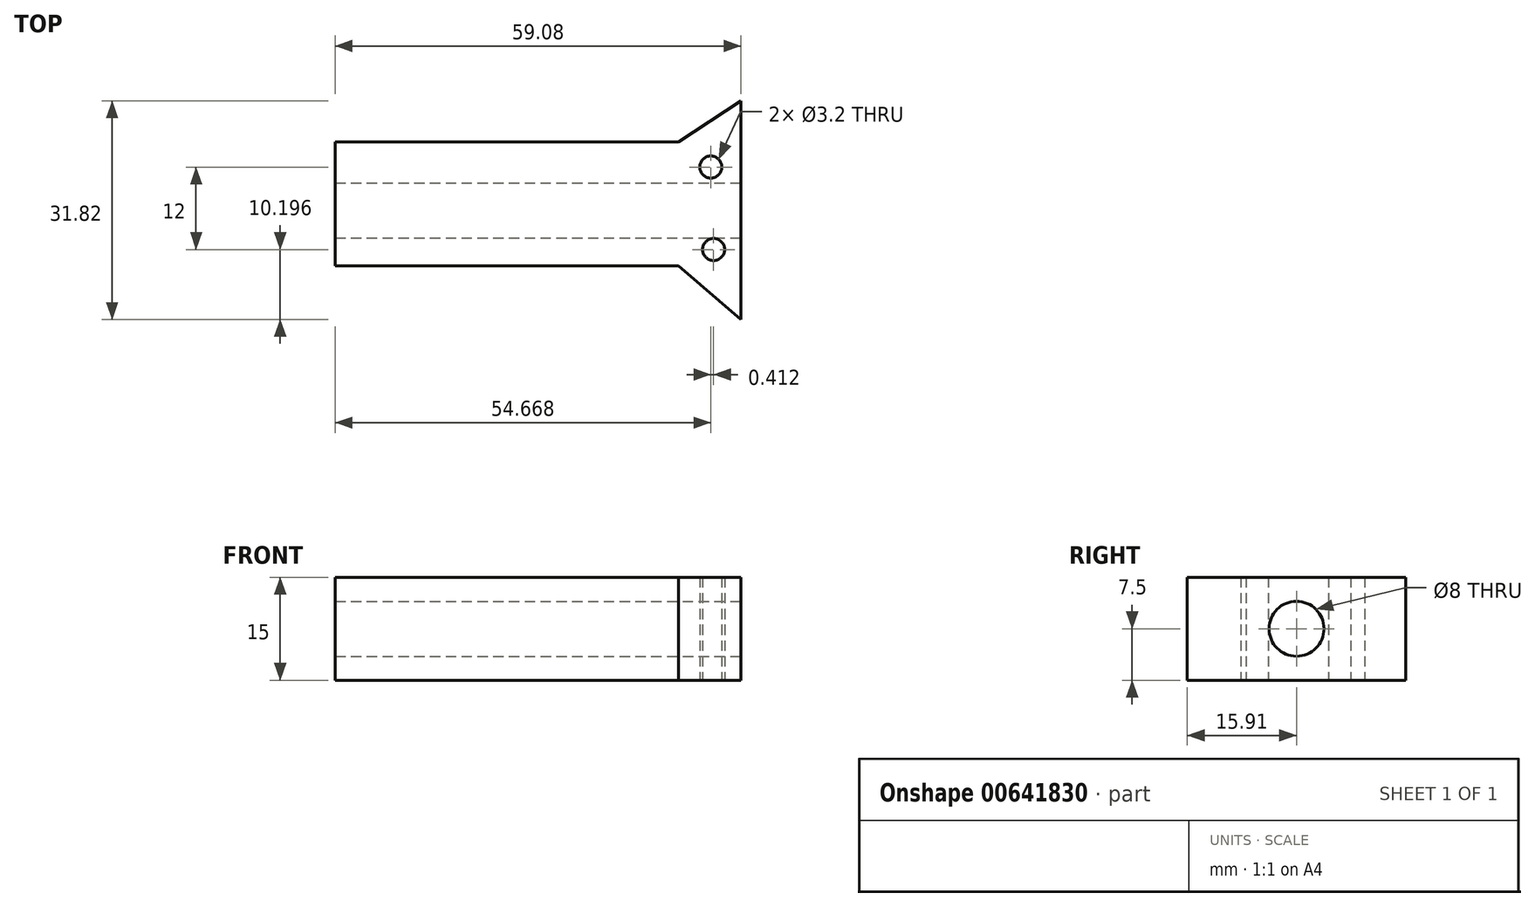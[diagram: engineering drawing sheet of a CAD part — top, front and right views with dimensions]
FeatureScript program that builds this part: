
annotation { "Feature Type Name" : "Feature", "Feature Type Description" : "" }
export const myFeature = defineFeature(function(context is Context, id is Id, definition is map)
    precondition{}
    {
        {
            var Q0;
            Q0=qCreatedBy(makeId("Top.planeOp"),FACE);
            var sketch = newSketch(context, id + "F0", { "sketchPlane" : qUnion([Q0])});
            skLineSegment(sketch, "E0.left", {"start": v(-5.08, -22.24) * mm, "end": v(-5.08, -4.24) * mm});
            skLineSegment(sketch, "E0.right", {"start": v(4, -30.06) * mm, "end": v(4, 1.76) * mm});
            skLineSegment(sketch, "E1", {"start": v(4, -30.06) * mm, "end": v(-5.08, -22.24) * mm});
            skLineSegment(sketch, "E2", {"start": v(-5.08, -4.24) * mm, "end": v(4, 1.76) * mm});
            skCircle(sketch, "E3", {"center": v(0, -19.86) * mm, "radius": 1.6 * mm});
            skCircle(sketch, "E4", {"center": v(-0.41, -7.86) * mm, "radius": 1.6 * mm});
            skSolve(sketch);
        }
        {
            var Q0;
            Q0 = qSketchRegion(id + "F0", true);
            extrude(context, id + "F1", {"entities" : qUnion([Q0]), "depth" : 15 * mm, "offsetDistance" : 25 * mm, "symmetric" : true});
        }
        {
            var Q0;
            Q0=makeQuery(id+"F1.opExtrude","SWEPT_FACE",FACE,{"disambiguationData":[OSD([sQuery(id+"F0.wireOp",EDGE,"E0.left")])]});
            extrude(context, id + "F2", {"entities" : qUnion([Q0]), "operationType" : NewBodyOperationType.ADD, "depth" : 50 * mm, "offsetDistance" : 25 * mm});
        }
        {
            var Q0;
            Q0=makeQuery(id+"F1.opExtrude","SWEPT_FACE",FACE,{"disambiguationData":[OSD([sQuery(id+"F0.wireOp",EDGE,"E0.right")])]});
            var sketch = newSketch(context, id + "F3", { "sketchPlane" : qUnion([Q0])});
            skCircle(sketch, "E5", {"center": v(-14.15, 0) * mm, "radius": 4 * mm});
            skPoint(sketch, "E5.centerSnap0", {"position": v(-14.15, -7.5) * mm});
            skSolve(sketch);
        }
        {
            var Q0;
            Q0=makeQuery(id+"F3.imprint","IMPRINT",FACE,{"disambiguationData":[TD([[makeQuery(id+"F3.imprint","IMPRINT",EDGE,{"derivedFrom":sQuery(id+"F3.wireOp",EDGE,"E5")}),1.0]])]});
            extrude(context, id + "F4", {"entities" : qUnion([Q0]), "operationType" : NewBodyOperationType.REMOVE, "endBound" : BoundingType.THROUGH_ALL, "oppositeDirection" : true, "depth" : 25 * mm, "offsetDistance" : 25 * mm});
        }
    });
